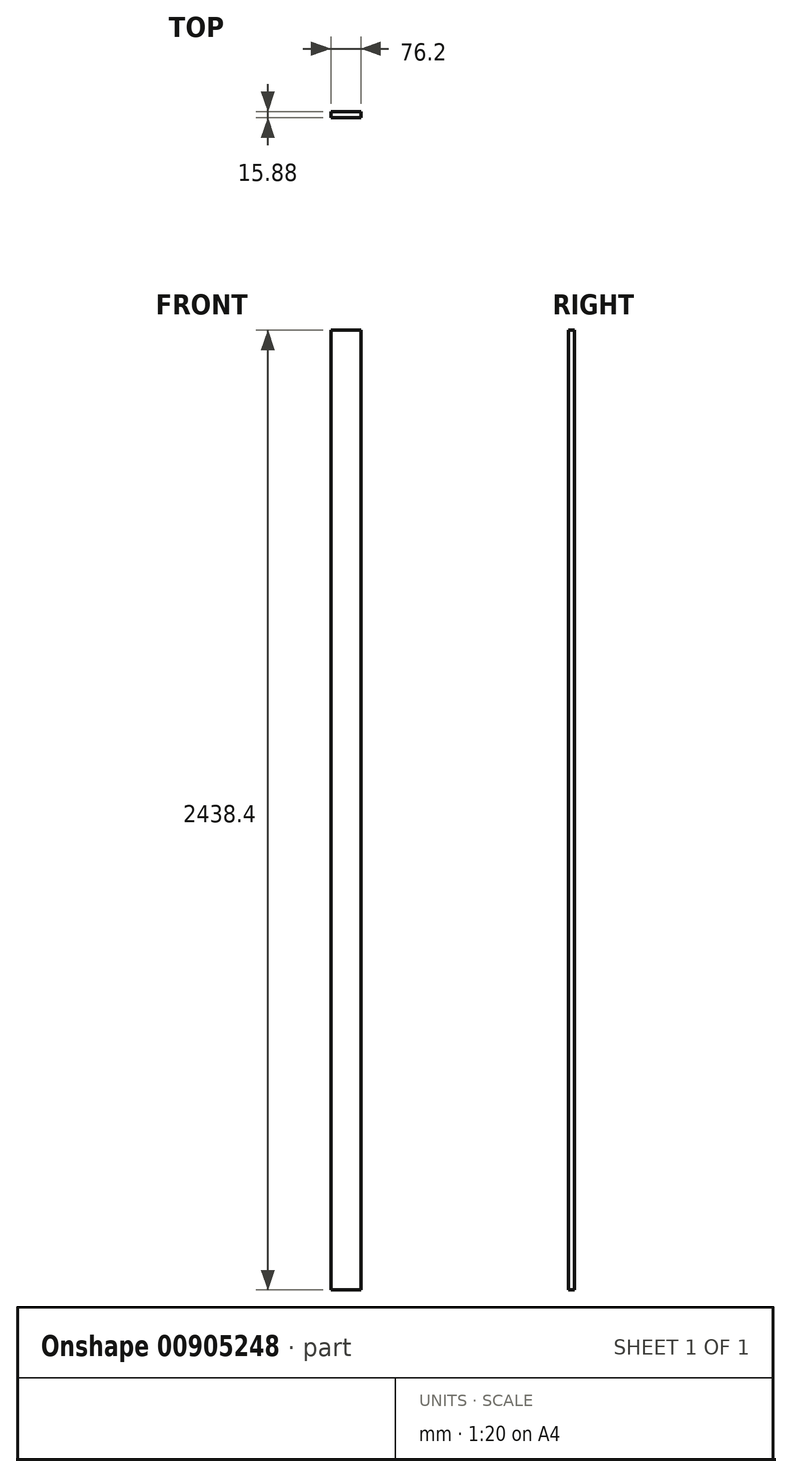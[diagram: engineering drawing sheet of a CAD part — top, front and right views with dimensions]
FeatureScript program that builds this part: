
annotation { "Feature Type Name" : "Feature", "Feature Type Description" : "" }
export const myFeature = defineFeature(function(context is Context, id is Id, definition is map)
    precondition{}
    {
        {
            var Q0;
            Q0=qCreatedBy(makeId("Front.planeOp"),FACE);
            var sketch = newSketch(context, id + "F0", { "sketchPlane" : qUnion([Q0])});
            skLineSegment(sketch, "E0.bottom", {"start": v(38.1, -1219.2) * mm, "end": v(-38.1, -1219.2) * mm});
            skLineSegment(sketch, "E0.top", {"start": v(38.1, 1219.2) * mm, "end": v(-38.1, 1219.2) * mm});
            skLineSegment(sketch, "E0.left", {"start": v(38.1, -1219.2) * mm, "end": v(38.1, 1219.2) * mm});
            skLineSegment(sketch, "E0.right", {"start": v(-38.1, -1219.2) * mm, "end": v(-38.1, 1219.2) * mm});
            skPoint(sketch, "E0.middle", {"position": v(0, 0) * mm});
            skSolve(sketch);
        }
        {
            var Q0;
            Q0=qSketchRegion(id+"F0",true);
            extrude(context, id + "F1", {"entities" : qUnion([Q0]), "oppositeDirection" : true, "depth" : 15.88 * mm});
        }
    });
